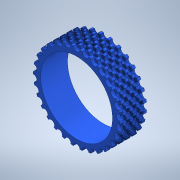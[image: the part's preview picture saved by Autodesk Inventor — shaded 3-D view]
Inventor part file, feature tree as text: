
AUTODESK INVENTOR PART (.ipt)
format: ipt  version: 2020 (Build 240168000, 168)  size: 941,568 bytes
history: native  units: in
note: dims shown in document units (in); Inventor stores cm internally (conversion verified against a paired STEP export)
features: extrude x3, sketch x3, pattern_circular x2, pattern_linear x1
ambient origin geometry x8: Origin, YZ Plane, XZ Plane, XY Plane, X Axis, Y Axis, Z Axis, Center Point
bodies: Solid1 (feature_tree)
feature tree (9):
  extrude  "Extrusion1"  Depth=1.0in
  extrude  "Extrusion2"  Depth=0.125in
  pattern_circular  "Circular Pattern3"  Count=30 Angle=360.0deg
  extrude  "Extrusion4"  Depth=0.125in
  pattern_circular  "Circular Pattern4"  [2 undecoded]
  pattern_linear  "Rectangular Pattern2"  Count1=30 Spacing1=360.0deg
  sketch  "Sketch1"  dims[d1=1.0in d2=0.0in d3=0.28in]
  sketch  "Sketch3"  dims[d4=2.686in d5=0.125in]
  sketch  "Sketch5"  dims[d6=0.125in d7=0.0in d27=11.811in d28=360.0deg d30=0.125in d31=0.125in d32=0.0in d33=11.811in d34=360.0deg d36=1.5748in d38=0.25in]
note: 2 required parameter values undecoded (feature->parameter linkage not recoverable at this tier; creation-order binding heuristic only, values carry confidence <= 0.55)
